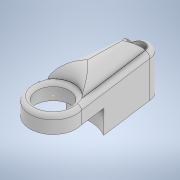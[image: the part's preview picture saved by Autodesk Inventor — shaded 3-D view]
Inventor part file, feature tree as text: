
AUTODESK INVENTOR PART (.ipt)
format: ipt  version: 2021 (Build 250183000, 183)  size: 217,600 bytes
history: native  units: mm
features: sketch x8, extrude x7, fillet x2, other x1
ambient origin geometry x8: Origin, YZ Plane, XZ Plane, XY Plane, X Axis, Y Axis, Z Axis, Center Point
bodies: Body1 (feature_tree)
feature tree (18):
  other  "Bryła1"
  extrude  "Wyciągnięcie proste1"  Depth=7.5mm TaperAngle=0.0deg
  extrude  "Wyciągnięcie proste2"  Depth=16.0mm
  extrude  "Wyciągnięcie proste3"  Depth=14.0mm
  extrude  "Wyciągnięcie proste4"  TaperAngle=0.0deg  [1 undecoded]
  sketch  "Szkic5"
  extrude  "Wyciągnięcie proste5"  Depth=16.0mm
  fillet  "Zaokrąglenie1"  Radius=6.0mm
  extrude  "Wyciągnięcie proste6"  TaperAngle=0.0deg  [1 undecoded]
  extrude  "Wyciągnięcie proste7"  Depth=27.0mm
  fillet  "Zaokrąglenie2"  Radius=32.0mm
  sketch  "Szkic1"
  sketch  "Szkic2"
  sketch  "Szkic3"
  sketch  "Szkic4"
  sketch  "Szkic6"
  sketch  "Szkic7"
  sketch  "Szkic8"
note: 2 required parameter values undecoded (feature->parameter linkage not recoverable at this tier; creation-order binding heuristic only, values carry confidence <= 0.55)
